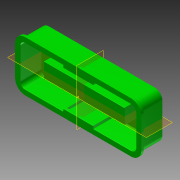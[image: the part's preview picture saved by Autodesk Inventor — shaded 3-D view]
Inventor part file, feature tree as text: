
AUTODESK INVENTOR PART (.ipt)
format: ipt  version: 2015 (Build 190159000, 159)  size: 243,200 bytes
history: native  units: in
note: dims shown in document units (in); Inventor stores cm internally (conversion verified against a paired STEP export)
features: fillet x7, sketch x6, extrude x5, mirror x4, plane x3, shell x2
ambient origin geometry x8: Origin, YZ Plane, XZ Plane, XY Plane, X Axis, Y Axis, Z Axis, Center Point
bodies: Solid1 (feature_tree)
feature tree (27):
  extrude  "Extrusion1"  Depth=0.5in
  fillet  "Fillet1"  Radius=0.47in
  shell  "Shell1"  Thickness=0.2in
  sketch  "Sketch2"  dims[d7=0.46in d8=0.2283in]
  plane  "Work Plane1"
  shell  "Shell2"  Thickness=0.1in
  extrude  "Extrusion5"  Depth=0.2283in
  plane  "Work Plane3"
  extrude  "Extrusion6"  Depth=0.47in TaperAngle=0.0deg
  plane  "Work Plane4"
  extrude  "Extrusion7"  Depth=0.01in
  fillet  "Fillet8"  Radius=0.05in
  mirror  "Mirror3"
  mirror  "Mirror4"
  sketch  "Sketch7"  dims[d34=0.03in d35=0.4325in d36=0.0in d37=0.3in d38=0.8in d39=0.15in d40=0.005in d41=0.0in d42=0.005in]
  fillet  "Fillet6"  Radius=0.05in
  fillet  "Fillet3"  Radius=0.445in
  fillet  "Fillet4"  Radius=0.05in
  extrude  "Extrusion2"  Depth=0.05in TaperAngle=0.0deg
  fillet  "Fillet2"  [1 undecoded]
  fillet  "Fillet7"  Radius=0.05in
  mirror  "Mirror1"
  mirror  "Mirror2"
  sketch  "Sketch1"  dims[d0=1.25in d1=0.5in d2=0.47in d3=0.0in d4=0.2in d5=0.1in]
  sketch  "Sketch4"  dims[d9=-0.033in d10=0.47in d11=0.0in]
  sketch  "Sketch5"  dims[d12=0.005in d13=0.01in d18=0.05in d23=0.05in d26=0.445in d28=0.05in]
  sketch  "Sketch6"  dims[d29=0.3in d30=0.05in d31=0.0in d32=-0.05in d33=0.05in]
note: 1 required parameter value undecoded (feature->parameter linkage not recoverable at this tier; creation-order binding heuristic only, values carry confidence <= 0.55)
